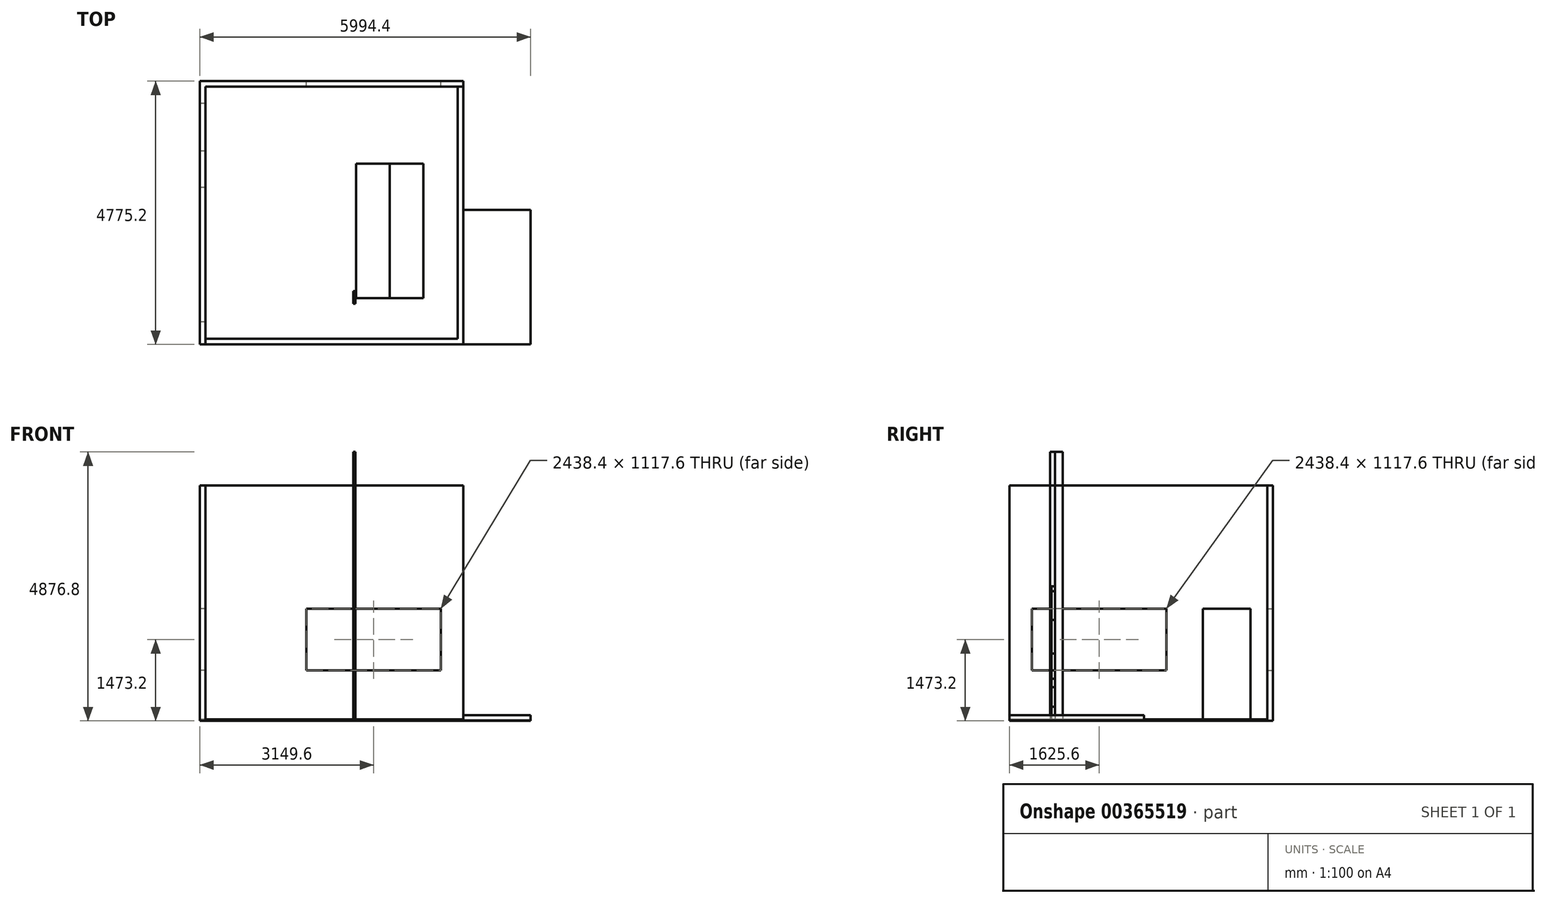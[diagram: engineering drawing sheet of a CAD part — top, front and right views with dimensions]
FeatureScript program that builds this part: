
annotation { "Feature Type Name" : "Feature", "Feature Type Description" : "" }
export const myFeature = defineFeature(function(context is Context, id is Id, definition is map)
    precondition{}
    {
        {
            var Q0;
            Q0=qCreatedBy(makeId("Top.planeOp"),FACE);
            var sketch = newSketch(context, id + "F0", { "sketchPlane" : qUnion([Q0])});
            skLineSegment(sketch, "E0.bottom", {"start": v(-51.8, 152.53) * mm, "end": v(37.1, 152.53) * mm});
            skLineSegment(sketch, "E0.top", {"start": v(-51.8, -101.47) * mm, "end": v(37.1, -101.47) * mm});
            skLineSegment(sketch, "E0.left", {"start": v(-51.8, 152.53) * mm, "end": v(-51.8, -101.47) * mm});
            skLineSegment(sketch, "E0.right", {"start": v(37.1, 152.53) * mm, "end": v(37.1, -101.47) * mm});
            skLineSegment(sketch, "E1", {"start": v(11.7, 152.53) * mm, "end": v(11.7, 12.83) * mm});
            skLineSegment(sketch, "E2", {"start": v(11.7, 12.83) * mm, "end": v(-51.8, 12.83) * mm});
            skLineSegment(sketch, "E3", {"start": v(-13.7, 152.53) * mm, "end": v(-13.7, 63.63) * mm});
            skLineSegment(sketch, "E4", {"start": v(-13.7, 63.63) * mm, "end": v(-51.8, 63.63) * mm});
            skLineSegment(sketch, "E5", {"start": v(-32.75, 152.53) * mm, "end": v(-32.75, 89.03) * mm});
            skLineSegment(sketch, "E6", {"start": v(-32.75, 89.03) * mm, "end": v(-51.8, 89.03) * mm});
            skLineSegment(sketch, "E7", {"start": v(-32.75, 89.03) * mm, "end": v(-32.75, 12.83) * mm});
            skPoint(sketch, "E7.endSnap0", {"position": v(-32.75, 63.63) * mm});
            skLineSegment(sketch, "E8", {"start": v(-32.75, 89.03) * mm, "end": v(-13.7, 89.03) * mm});
            skLineSegment(sketch, "E9.bottom", {"start": v(-51.8, 152.53) * mm, "end": v(-13.7, 152.53) * mm});
            skLineSegment(sketch, "E9.top", {"start": v(-51.8, 292.23) * mm, "end": v(-13.7, 292.23) * mm});
            skLineSegment(sketch, "E9.left", {"start": v(-51.8, 152.53) * mm, "end": v(-51.8, 292.23) * mm});
            skLineSegment(sketch, "E9.right", {"start": v(-13.7, 152.53) * mm, "end": v(-13.7, 292.23) * mm});
            skSolve(sketch);
        }
        {
            var Q0;
            {var subQ3=sQuery(id+"F0.wireOp",EDGE,"E5");Q0=makeQuery(id+"F0.imprint","IMPRINT",FACE,{"disambiguationData":[TD([[makeQuery(id+"F0.imprint","IMPRINT",EDGE,{"derivedFrom":subQ3}),-1.0]])]});}
            extrude(context, id + "F1", {"entities" : qUnion([Q0]), "depth" : 2438.4 * mm, "offsetDistance" : 25.4 * mm});
        }
        {
            var Q0;
            {var subQ3=sQuery(id+"F0.wireOp",EDGE,"E5");Q0=makeQuery(id+"F0.imprint","IMPRINT",FACE,{"disambiguationData":[TD([[makeQuery(id+"F0.imprint","IMPRINT",EDGE,{"derivedFrom":subQ3}),-1.0]])]});}
            var Q1;
            {var subQ3=sQuery(id+"F0.wireOp",EDGE,"E6");Q1=makeQuery(id+"F0.imprint","IMPRINT",FACE,{"disambiguationData":[TD([[makeQuery(id+"F0.imprint","IMPRINT",EDGE,{"derivedFrom":subQ3}),1.0]])]});}
            extrude(context, id + "F2", {"entities" : qUnion([Q0, Q1]), "depth" : 2438.4 * mm, "offsetDistance" : 25.4 * mm});
        }
        {
            var Q0;
            {var subQ3=sQuery(id+"F0.wireOp",EDGE,"E5");Q0=makeQuery(id+"F0.imprint","IMPRINT",FACE,{"disambiguationData":[TD([[makeQuery(id+"F0.imprint","IMPRINT",EDGE,{"derivedFrom":subQ3}),-1.0]])]});}
            var Q1;
            {var subQ3=sQuery(id+"F0.wireOp",EDGE,"E5");Q1=makeQuery(id+"F0.imprint","IMPRINT",FACE,{"disambiguationData":[TD([[makeQuery(id+"F0.imprint","IMPRINT",EDGE,{"derivedFrom":subQ3}),1.0]])]});}
            extrude(context, id + "F3", {"entities" : qUnion([Q0, Q1]), "depth" : 2438.4 * mm, "offsetDistance" : 25.4 * mm});
        }
        {
            var Q0;
            {var subQ3=sQuery(id+"F0.wireOp",EDGE,"E5");Q0=makeQuery(id+"F0.imprint","IMPRINT",FACE,{"disambiguationData":[TD([[makeQuery(id+"F0.imprint","IMPRINT",EDGE,{"derivedFrom":subQ3}),-1.0]])]});}
            var Q1;
            {var subQ3=sQuery(id+"F0.wireOp",EDGE,"E5");Q1=makeQuery(id+"F0.imprint","IMPRINT",FACE,{"disambiguationData":[TD([[makeQuery(id+"F0.imprint","IMPRINT",EDGE,{"derivedFrom":subQ3}),1.0]])]});}
            var Q2;
            {var subQ3=sQuery(id+"F0.wireOp",EDGE,"E6");Q2=makeQuery(id+"F0.imprint","IMPRINT",FACE,{"disambiguationData":[TD([[makeQuery(id+"F0.imprint","IMPRINT",EDGE,{"derivedFrom":subQ3}),1.0]])]});}
            var Q3;
            {var subQ3=sQuery(id+"F0.wireOp",EDGE,"E8");Q3=makeQuery(id+"F0.imprint","IMPRINT",FACE,{"disambiguationData":[TD([[makeQuery(id+"F0.imprint","IMPRINT",EDGE,{"derivedFrom":subQ3}),-1.0]])]});}
            extrude(context, id + "F4", {"entities" : qUnion([Q0, Q1, Q2, Q3]), "depth" : 2438.4 * mm, "offsetDistance" : 25.4 * mm});
        }
        {
            var Q0;
            {var subQ3=sQuery(id+"F0.wireOp",EDGE,"E5");Q0=makeQuery(id+"F0.imprint","IMPRINT",FACE,{"disambiguationData":[TD([[makeQuery(id+"F0.imprint","IMPRINT",EDGE,{"derivedFrom":subQ3}),-1.0]])]});}
            var Q1;
            {var subQ3=sQuery(id+"F0.wireOp",EDGE,"E5");Q1=makeQuery(id+"F0.imprint","IMPRINT",FACE,{"disambiguationData":[TD([[makeQuery(id+"F0.imprint","IMPRINT",EDGE,{"derivedFrom":subQ3}),1.0]])]});}
            var Q2;
            {var subQ3=sQuery(id+"F0.wireOp",EDGE,"E8");Q2=makeQuery(id+"F0.imprint","IMPRINT",FACE,{"disambiguationData":[TD([[makeQuery(id+"F0.imprint","IMPRINT",EDGE,{"derivedFrom":subQ3}),-1.0]])]});}
            var Q3;
            {var subQ3=sQuery(id+"F0.wireOp",EDGE,"E6");Q3=makeQuery(id+"F0.imprint","IMPRINT",FACE,{"disambiguationData":[TD([[makeQuery(id+"F0.imprint","IMPRINT",EDGE,{"derivedFrom":subQ3}),1.0]])]});}
            extrude(context, id + "F5", {"entities" : qUnion([Q0, Q1, Q2, Q3]), "depth" : 914.4 * mm, "offsetDistance" : 25.4 * mm});
        }
        {
            var Q0;
            {var subQ3=sQuery(id+"F0.wireOp",EDGE,"E5");Q0=makeQuery(id+"F0.imprint","IMPRINT",FACE,{"disambiguationData":[TD([[makeQuery(id+"F0.imprint","IMPRINT",EDGE,{"derivedFrom":subQ3}),-1.0]])]});}
            var Q1;
            {var subQ3=sQuery(id+"F0.wireOp",EDGE,"E5");Q1=makeQuery(id+"F0.imprint","IMPRINT",FACE,{"disambiguationData":[TD([[makeQuery(id+"F0.imprint","IMPRINT",EDGE,{"derivedFrom":subQ3}),1.0]])]});}
            var Q2;
            {var subQ3=sQuery(id+"F0.wireOp",EDGE,"E8");Q2=makeQuery(id+"F0.imprint","IMPRINT",FACE,{"disambiguationData":[TD([[makeQuery(id+"F0.imprint","IMPRINT",EDGE,{"derivedFrom":subQ3}),-1.0]])]});}
            var Q3;
            {var subQ3=sQuery(id+"F0.wireOp",EDGE,"E6");Q3=makeQuery(id+"F0.imprint","IMPRINT",FACE,{"disambiguationData":[TD([[makeQuery(id+"F0.imprint","IMPRINT",EDGE,{"derivedFrom":subQ3}),1.0]])]});}
            extrude(context, id + "F6", {"entities" : qUnion([Q0, Q1, Q2, Q3]), "depth" : 1219.2 * mm, "offsetDistance" : 25.4 * mm});
        }
        {
            var Q0;
            {var subQ3=sQuery(id+"F0.wireOp",EDGE,"E5");Q0=makeQuery(id+"F0.imprint","IMPRINT",FACE,{"disambiguationData":[TD([[makeQuery(id+"F0.imprint","IMPRINT",EDGE,{"derivedFrom":subQ3}),-1.0]])]});}
            var Q1;
            {var subQ3=sQuery(id+"F0.wireOp",EDGE,"E5");Q1=makeQuery(id+"F0.imprint","IMPRINT",FACE,{"disambiguationData":[TD([[makeQuery(id+"F0.imprint","IMPRINT",EDGE,{"derivedFrom":subQ3}),1.0]])]});}
            var Q2;
            {var subQ3=sQuery(id+"F0.wireOp",EDGE,"E8");Q2=makeQuery(id+"F0.imprint","IMPRINT",FACE,{"disambiguationData":[TD([[makeQuery(id+"F0.imprint","IMPRINT",EDGE,{"derivedFrom":subQ3}),-1.0]])]});}
            var Q3;
            {var subQ3=sQuery(id+"F0.wireOp",EDGE,"E6");Q3=makeQuery(id+"F0.imprint","IMPRINT",FACE,{"disambiguationData":[TD([[makeQuery(id+"F0.imprint","IMPRINT",EDGE,{"derivedFrom":subQ3}),1.0]])]});}
            extrude(context, id + "F7", {"entities" : qUnion([Q0, Q1, Q2, Q3]), "depth" : 1828.8 * mm, "offsetDistance" : 25.4 * mm});
        }
        {
            var Q0;
            {var subQ3=sQuery(id+"F0.wireOp",EDGE,"E5");Q0=makeQuery(id+"F0.imprint","IMPRINT",FACE,{"disambiguationData":[TD([[makeQuery(id+"F0.imprint","IMPRINT",EDGE,{"derivedFrom":subQ3}),-1.0]])]});}
            var Q1;
            {var subQ3=sQuery(id+"F0.wireOp",EDGE,"E5");Q1=makeQuery(id+"F0.imprint","IMPRINT",FACE,{"disambiguationData":[TD([[makeQuery(id+"F0.imprint","IMPRINT",EDGE,{"derivedFrom":subQ3}),1.0]])]});}
            var Q2;
            {var subQ3=sQuery(id+"F0.wireOp",EDGE,"E8");Q2=makeQuery(id+"F0.imprint","IMPRINT",FACE,{"disambiguationData":[TD([[makeQuery(id+"F0.imprint","IMPRINT",EDGE,{"derivedFrom":subQ3}),-1.0]])]});}
            var Q3;
            {var subQ3=sQuery(id+"F0.wireOp",EDGE,"E6");Q3=makeQuery(id+"F0.imprint","IMPRINT",FACE,{"disambiguationData":[TD([[makeQuery(id+"F0.imprint","IMPRINT",EDGE,{"derivedFrom":subQ3}),1.0]])]});}
            extrude(context, id + "F8", {"entities" : qUnion([Q0, Q1, Q2, Q3]), "depth" : 609.6 * mm, "offsetDistance" : 25.4 * mm});
        }
        {
            var Q0;
            {var subQ3=sQuery(id+"F0.wireOp",EDGE,"E5");Q0=makeQuery(id+"F0.imprint","IMPRINT",FACE,{"disambiguationData":[TD([[makeQuery(id+"F0.imprint","IMPRINT",EDGE,{"derivedFrom":subQ3}),-1.0]])]});}
            var Q1;
            {var subQ3=sQuery(id+"F0.wireOp",EDGE,"E5");Q1=makeQuery(id+"F0.imprint","IMPRINT",FACE,{"disambiguationData":[TD([[makeQuery(id+"F0.imprint","IMPRINT",EDGE,{"derivedFrom":subQ3}),1.0]])]});}
            extrude(context, id + "F9", {"entities" : qUnion([Q0, Q1]), "depth" : 1828.8 * mm, "offsetDistance" : 25.4 * mm});
        }
        {
            var Q0;
            {var subQ3=sQuery(id+"F0.wireOp",EDGE,"E5");Q0=makeQuery(id+"F0.imprint","IMPRINT",FACE,{"disambiguationData":[TD([[makeQuery(id+"F0.imprint","IMPRINT",EDGE,{"derivedFrom":subQ3}),-1.0]])]});}
            var Q1;
            {var subQ3=sQuery(id+"F0.wireOp",EDGE,"E5");Q1=makeQuery(id+"F0.imprint","IMPRINT",FACE,{"disambiguationData":[TD([[makeQuery(id+"F0.imprint","IMPRINT",EDGE,{"derivedFrom":subQ3}),1.0]])]});}
            extrude(context, id + "F10", {"entities" : qUnion([Q0, Q1]), "depth" : 1219.2 * mm, "offsetDistance" : 25.4 * mm});
        }
        {
            var Q0;
            {var subQ3=sQuery(id+"F0.wireOp",EDGE,"E5");Q0=makeQuery(id+"F0.imprint","IMPRINT",FACE,{"disambiguationData":[TD([[makeQuery(id+"F0.imprint","IMPRINT",EDGE,{"derivedFrom":subQ3}),-1.0]])]});}
            var Q1;
            {var subQ3=sQuery(id+"F0.wireOp",EDGE,"E5");Q1=makeQuery(id+"F0.imprint","IMPRINT",FACE,{"disambiguationData":[TD([[makeQuery(id+"F0.imprint","IMPRINT",EDGE,{"derivedFrom":subQ3}),1.0]])]});}
            extrude(context, id + "F11", {"entities" : qUnion([Q0, Q1]), "depth" : 914.4 * mm, "offsetDistance" : 25.4 * mm});
        }
        {
            var Q0;
            {var subQ3=sQuery(id+"F0.wireOp",EDGE,"E5");Q0=makeQuery(id+"F0.imprint","IMPRINT",FACE,{"disambiguationData":[TD([[makeQuery(id+"F0.imprint","IMPRINT",EDGE,{"derivedFrom":subQ3}),-1.0]])]});}
            var Q1;
            {var subQ3=sQuery(id+"F0.wireOp",EDGE,"E5");Q1=makeQuery(id+"F0.imprint","IMPRINT",FACE,{"disambiguationData":[TD([[makeQuery(id+"F0.imprint","IMPRINT",EDGE,{"derivedFrom":subQ3}),1.0]])]});}
            extrude(context, id + "F12", {"entities" : qUnion([Q0, Q1]), "depth" : 609.6 * mm, "offsetDistance" : 25.4 * mm});
        }
        {
            var Q0;
            {var subQ3=sQuery(id+"F0.wireOp",EDGE,"E5");Q0=makeQuery(id+"F0.imprint","IMPRINT",FACE,{"disambiguationData":[TD([[makeQuery(id+"F0.imprint","IMPRINT",EDGE,{"derivedFrom":subQ3}),-1.0]])]});}
            var Q1;
            {var subQ3=sQuery(id+"F0.wireOp",EDGE,"E5");Q1=makeQuery(id+"F0.imprint","IMPRINT",FACE,{"disambiguationData":[TD([[makeQuery(id+"F0.imprint","IMPRINT",EDGE,{"derivedFrom":subQ3}),1.0]])]});}
            extrude(context, id + "F13", {"entities" : qUnion([Q0, Q1]), "depth" : 762 * mm, "offsetDistance" : 25.4 * mm});
        }
        {
            var Q0;
            {var subQ3=sQuery(id+"F0.wireOp",EDGE,"E8");Q0=makeQuery(id+"F0.imprint","IMPRINT",FACE,{"disambiguationData":[TD([[makeQuery(id+"F0.imprint","IMPRINT",EDGE,{"derivedFrom":subQ3}),-1.0]])]});}
            var Q1;
            {var subQ3=sQuery(id+"F0.wireOp",EDGE,"E6");Q1=makeQuery(id+"F0.imprint","IMPRINT",FACE,{"disambiguationData":[TD([[makeQuery(id+"F0.imprint","IMPRINT",EDGE,{"derivedFrom":subQ3}),1.0]])]});}
            extrude(context, id + "F14", {"entities" : qUnion([Q0, Q1]), "depth" : 1828.8 * mm, "offsetDistance" : 25.4 * mm});
        }
        {
            var Q0;
            Q0=qCreatedBy(makeId("Top.planeOp"),FACE);
            var sketch = newSketch(context, id + "F15", { "sketchPlane" : qUnion([Q0])});
            skLineSegment(sketch, "E10.bottom", {"start": v(-2730.57, 3997.99) * mm, "end": v(1841.43, 3997.99) * mm});
            skLineSegment(sketch, "E10.top", {"start": v(-2730.57, -574.01) * mm, "end": v(1841.43, -574.01) * mm});
            skLineSegment(sketch, "E10.left", {"start": v(-2730.57, 3997.99) * mm, "end": v(-2730.57, -574.01) * mm});
            skLineSegment(sketch, "E10.right", {"start": v(1841.43, 3997.99) * mm, "end": v(1841.43, -574.01) * mm});
            skLineSegment(sketch, "E11.bottom", {"start": v(1943.03, -675.61) * mm, "end": v(3162.23, -675.61) * mm});
            skLineSegment(sketch, "E11.top", {"start": v(1943.03, 1762.79) * mm, "end": v(3162.23, 1762.79) * mm});
            skLineSegment(sketch, "E11.right", {"start": v(3162.23, -675.61) * mm, "end": v(3162.23, 1762.79) * mm});
            skLineSegment(sketch, "E12.0", {"start": v(-2832.17, 4099.59) * mm, "end": v(-2832.17, -675.61) * mm});
            skLineSegment(sketch, "E12.1", {"start": v(-2832.17, 4099.59) * mm, "end": v(1943.03, 4099.59) * mm});
            skLineSegment(sketch, "E12.2", {"start": v(1943.03, 4099.59) * mm, "end": v(1943.03, -675.61) * mm});
            skLineSegment(sketch, "E12.3", {"start": v(-2832.17, -675.61) * mm, "end": v(1943.03, -675.61) * mm});
            skLineSegment(sketch, "E13", {"start": v(-2730.57, 3693.19) * mm, "end": v(-2832.17, 3693.19) * mm});
            skLineSegment(sketch, "E14.0", {"start": v(-2730.57, 2829.59) * mm, "end": v(-2832.17, 2829.59) * mm});
            skLineSegment(sketch, "E15", {"start": v(1841.43, 3997.99) * mm, "end": v(1943.03, 3997.99) * mm});
            skLineSegment(sketch, "E16", {"start": v(-2730.57, -574.01) * mm, "end": v(-2730.57, -675.61) * mm});
            skLineSegment(sketch, "E17", {"start": v(-901.77, 3997.99) * mm, "end": v(-901.77, 4099.59) * mm});
            skLineSegment(sketch, "E18", {"start": v(-2730.57, 2169.19) * mm, "end": v(-2832.17, 2169.19) * mm});
            skLineSegment(sketch, "E19.0", {"start": v(1536.63, 3997.99) * mm, "end": v(1536.63, 4099.59) * mm});
            skLineSegment(sketch, "E20.0", {"start": v(-2730.57, -269.21) * mm, "end": v(-2832.17, -269.21) * mm});
            skSolve(sketch);
        }
        {
            var Q0;
            Q0=makeQuery(id+"F15.imprint","IMPRINT",FACE,{"disambiguationData":[TD([[makeQuery(id+"F15.imprint","IMPRINT",EDGE,{"derivedFrom":sQuery(id+"F15.wireOp",EDGE,"E10.bottom")}),-1.0]])]});
            var Q1;
            {var subQ0=sQuery(id+"F15.wireOp",EDGE,"E13");Q1=makeQuery(id+"F15.imprint","IMPRINT",FACE,{"disambiguationData":[TD([[makeQuery(id+"F15.imprint","IMPRINT",EDGE,{"derivedFrom":subQ0}),1.0]])]});}
            extrude(context, id + "F16", {"entities" : qUnion([Q0, Q1]), "depth" : 25.4 * mm, "offsetDistance" : 25.4 * mm});
        }
        {
            var Q0;
            Q0=makeQuery(id+"F15.imprint","IMPRINT",FACE,{"disambiguationData":[TD([[makeQuery(id+"F15.imprint","IMPRINT",EDGE,{"derivedFrom":sQuery(id+"F15.wireOp",EDGE,"E11.bottom")}),1.0]])]});
            extrude(context, id + "F17", {"entities" : qUnion([Q0]), "depth" : 6.35 * mm, "offsetDistance" : 25.4 * mm});
        }
        {
            var Q0;
            {var subQ0=sQuery(id+"F15.wireOp",EDGE,"E14.0");Q0=makeQuery(id+"F15.imprint","IMPRINT",FACE,{"disambiguationData":[TD([[makeQuery(id+"F15.imprint","IMPRINT",EDGE,{"derivedFrom":subQ0}),1.0]])]});}
            var Q1;
            {var subQ0=sQuery(id+"F15.wireOp",EDGE,"E15");Q1=makeQuery(id+"F15.imprint","IMPRINT",FACE,{"disambiguationData":[TD([[makeQuery(id+"F15.imprint","IMPRINT",EDGE,{"derivedFrom":subQ0}),1.0]])]});}
            var Q2;
            {var subQ4=sQuery(id+"F15.wireOp",EDGE,"E13");Q2=makeQuery(id+"F15.imprint","IMPRINT",FACE,{"disambiguationData":[TD([[makeQuery(id+"F15.imprint","IMPRINT",EDGE,{"derivedFrom":subQ4}),-1.0]])]});}
            var Q3;
            {var subQ0=sQuery(id+"F15.wireOp",EDGE,"E16");Q3=makeQuery(id+"F15.imprint","IMPRINT",FACE,{"disambiguationData":[TD([[makeQuery(id+"F15.imprint","IMPRINT",EDGE,{"derivedFrom":subQ0}),-1.0]])]});}
            extrude(context, id + "F18", {"entities" : qUnion([Q0, Q1, Q2, Q3]), "operationType" : NewBodyOperationType.ADD, "depth" : 4267.2 * mm, "offsetDistance" : 25.4 * mm});
        }
        {
            var Q0;
            Q0=makeQuery(id+"F15.imprint","IMPRINT",FACE,{"disambiguationData":[TD([[makeQuery(id+"F15.imprint","IMPRINT",EDGE,{"derivedFrom":sQuery(id+"F15.wireOp",EDGE,"E10.top")}),-1.0]])]});
            extrude(context, id + "F19", {"entities" : qUnion([Q0]), "operationType" : NewBodyOperationType.ADD, "depth" : 27.94 * mm, "offsetDistance" : 25.4 * mm});
        }
        {
            var Q0;
            {var subQ0=sQuery(id+"F15.wireOp",EDGE,"E13");Q0=makeQuery(id+"F15.imprint","IMPRINT",FACE,{"disambiguationData":[TD([[makeQuery(id+"F15.imprint","IMPRINT",EDGE,{"derivedFrom":subQ0}),1.0]])]});}
            var Q1;
            {var subQ0=sQuery(id+"F15.wireOp",EDGE,"E18");Q1=makeQuery(id+"F15.imprint","IMPRINT",FACE,{"disambiguationData":[TD([[makeQuery(id+"F15.imprint","IMPRINT",EDGE,{"derivedFrom":subQ0}),1.0]])]});}
            var Q2;
            {var subQ0=sQuery(id+"F15.wireOp",EDGE,"E17");Q2=makeQuery(id+"F15.imprint","IMPRINT",FACE,{"disambiguationData":[TD([[makeQuery(id+"F15.imprint","IMPRINT",EDGE,{"derivedFrom":subQ0}),-1.0]])]});}
            extrude(context, id + "F20", {"entities" : qUnion([Q0, Q1, Q2]), "operationType" : NewBodyOperationType.ADD, "depth" : 4267.2 * mm, "offsetDistance" : 25.4 * mm, "hasSecondDirection" : true, "secondDirectionOppositeDirection" : false, "secondDirectionDepth" : 2032 * mm});
        }
        {
            var Q0;
            {var subQ0=sQuery(id+"F15.wireOp",EDGE,"E18");Q0=makeQuery(id+"F15.imprint","IMPRINT",FACE,{"disambiguationData":[TD([[makeQuery(id+"F15.imprint","IMPRINT",EDGE,{"derivedFrom":subQ0}),1.0]])]});}
            var Q1;
            {var subQ0=sQuery(id+"F15.wireOp",EDGE,"E17");Q1=makeQuery(id+"F15.imprint","IMPRINT",FACE,{"disambiguationData":[TD([[makeQuery(id+"F15.imprint","IMPRINT",EDGE,{"derivedFrom":subQ0}),-1.0]])]});}
            extrude(context, id + "F21", {"entities" : qUnion([Q0, Q1]), "operationType" : NewBodyOperationType.ADD, "depth" : 914.4 * mm, "offsetDistance" : 25.4 * mm});
        }
        {
            var Q0;
            {var subQ0=sQuery(id+"F15.wireOp",EDGE,"E11.bottom");Q0=makeQuery(id+"F15.imprint","IMPRINT",FACE,{"disambiguationData":[TD([[makeQuery(id+"F15.imprint","IMPRINT",EDGE,{"derivedFrom":subQ0}),1.0]])]});}
            extrude(context, id + "F22", {"entities" : qUnion([Q0]), "depth" : 101.6 * mm, "offsetDistance" : 25.4 * mm});
        }
        {
            var Q0;
            {var subQ3=sQuery(id+"F0.wireOp",EDGE,"E5");Q0=makeQuery(id+"F0.imprint","IMPRINT",FACE,{"disambiguationData":[TD([[makeQuery(id+"F0.imprint","IMPRINT",EDGE,{"derivedFrom":subQ3}),-1.0]])]});}
            var Q1;
            {var subQ3=sQuery(id+"F0.wireOp",EDGE,"E5");Q1=makeQuery(id+"F0.imprint","IMPRINT",FACE,{"disambiguationData":[TD([[makeQuery(id+"F0.imprint","IMPRINT",EDGE,{"derivedFrom":subQ3}),1.0]])]});}
            var Q2;
            {var subQ3=sQuery(id+"F0.wireOp",EDGE,"E6");Q2=makeQuery(id+"F0.imprint","IMPRINT",FACE,{"disambiguationData":[TD([[makeQuery(id+"F0.imprint","IMPRINT",EDGE,{"derivedFrom":subQ3}),1.0]])]});}
            var Q3;
            {var subQ3=sQuery(id+"F0.wireOp",EDGE,"E8");Q3=makeQuery(id+"F0.imprint","IMPRINT",FACE,{"disambiguationData":[TD([[makeQuery(id+"F0.imprint","IMPRINT",EDGE,{"derivedFrom":subQ3}),-1.0]])]});}
            extrude(context, id + "F23", {"entities" : qUnion([Q0, Q1, Q2, Q3]), "depth" : 2352.67 * mm, "offsetDistance" : 25.4 * mm});
        }
        {
            var Q0;
            Q0=makeQuery(id+"F0.imprint","IMPRINT",FACE,{"disambiguationData":[TD([[makeQuery(id+"F0.imprint","IMPRINT",EDGE,{"derivedFrom":sQuery(id+"F0.wireOp",EDGE,"E9.top")}),-1.0]])]});
            extrude(context, id + "F24", {"entities" : qUnion([Q0]), "depth" : 4267.2 * mm, "offsetDistance" : 25.4 * mm});
        }
        {
            var Q0;
            Q0=makeQuery(id+"F0.imprint","IMPRINT",FACE,{"disambiguationData":[TD([[makeQuery(id+"F0.imprint","IMPRINT",EDGE,{"derivedFrom":sQuery(id+"F0.wireOp",EDGE,"E9.top")}),-1.0]])]});
            extrude(context, id + "F25", {"entities" : qUnion([Q0]), "depth" : 4876.8 * mm, "offsetDistance" : 25.4 * mm});
        }
        {
            var Q0;
            {var subQ3=sQuery(id+"F0.wireOp",EDGE,"E6");Q0=makeQuery(id+"F0.imprint","IMPRINT",FACE,{"disambiguationData":[TD([[makeQuery(id+"F0.imprint","IMPRINT",EDGE,{"derivedFrom":subQ3}),1.0]])]});}
            var Q1;
            {var subQ4=sQuery(id+"F0.wireOp",EDGE,"E5");Q1=makeQuery(id+"F0.imprint","IMPRINT",FACE,{"disambiguationData":[TD([[makeQuery(id+"F0.imprint","IMPRINT",EDGE,{"derivedFrom":subQ4}),-1.0]])]});}
            var Q2;
            {var subQ4=sQuery(id+"F0.wireOp",EDGE,"E5");Q2=makeQuery(id+"F0.imprint","IMPRINT",FACE,{"disambiguationData":[TD([[makeQuery(id+"F0.imprint","IMPRINT",EDGE,{"derivedFrom":subQ4}),1.0]])]});}
            var Q3;
            {var subQ3=sQuery(id+"F0.wireOp",EDGE,"E8");Q3=makeQuery(id+"F0.imprint","IMPRINT",FACE,{"disambiguationData":[TD([[makeQuery(id+"F0.imprint","IMPRINT",EDGE,{"derivedFrom":subQ3}),-1.0]])]});}
            extrude(context, id + "F26", {"entities" : qUnion([Q0, Q1, Q2, Q3]), "depth" : 254 * mm, "offsetDistance" : 25.4 * mm});
        }
        {
            var Q0;
            {var subQ3=sQuery(id+"F0.wireOp",EDGE,"E6");Q0=makeQuery(id+"F0.imprint","IMPRINT",FACE,{"disambiguationData":[TD([[makeQuery(id+"F0.imprint","IMPRINT",EDGE,{"derivedFrom":subQ3}),1.0]])]});}
            var Q1;
            {var subQ4=sQuery(id+"F0.wireOp",EDGE,"E5");Q1=makeQuery(id+"F0.imprint","IMPRINT",FACE,{"disambiguationData":[TD([[makeQuery(id+"F0.imprint","IMPRINT",EDGE,{"derivedFrom":subQ4}),-1.0]])]});}
            var Q2;
            {var subQ4=sQuery(id+"F0.wireOp",EDGE,"E5");Q2=makeQuery(id+"F0.imprint","IMPRINT",FACE,{"disambiguationData":[TD([[makeQuery(id+"F0.imprint","IMPRINT",EDGE,{"derivedFrom":subQ4}),1.0]])]});}
            var Q3;
            {var subQ3=sQuery(id+"F0.wireOp",EDGE,"E8");Q3=makeQuery(id+"F0.imprint","IMPRINT",FACE,{"disambiguationData":[TD([[makeQuery(id+"F0.imprint","IMPRINT",EDGE,{"derivedFrom":subQ3}),-1.0]])]});}
            extrude(context, id + "F27", {"entities" : qUnion([Q0, Q1, Q2, Q3]), "depth" : 101.6 * mm, "offsetDistance" : 25.4 * mm});
        }
        {
            var Q0;
            {var subQ3=sQuery(id+"F0.wireOp",EDGE,"E6");Q0=makeQuery(id+"F0.imprint","IMPRINT",FACE,{"disambiguationData":[TD([[makeQuery(id+"F0.imprint","IMPRINT",EDGE,{"derivedFrom":subQ3}),1.0]])]});}
            var Q1;
            {var subQ4=sQuery(id+"F0.wireOp",EDGE,"E5");Q1=makeQuery(id+"F0.imprint","IMPRINT",FACE,{"disambiguationData":[TD([[makeQuery(id+"F0.imprint","IMPRINT",EDGE,{"derivedFrom":subQ4}),-1.0]])]});}
            var Q2;
            {var subQ4=sQuery(id+"F0.wireOp",EDGE,"E5");Q2=makeQuery(id+"F0.imprint","IMPRINT",FACE,{"disambiguationData":[TD([[makeQuery(id+"F0.imprint","IMPRINT",EDGE,{"derivedFrom":subQ4}),1.0]])]});}
            var Q3;
            {var subQ3=sQuery(id+"F0.wireOp",EDGE,"E8");Q3=makeQuery(id+"F0.imprint","IMPRINT",FACE,{"disambiguationData":[TD([[makeQuery(id+"F0.imprint","IMPRINT",EDGE,{"derivedFrom":subQ3}),-1.0]])]});}
            extrude(context, id + "F28", {"entities" : qUnion([Q0, Q1, Q2, Q3]), "depth" : 4876.8 * mm, "offsetDistance" : 25.4 * mm});
        }
        {
            var Q0;
            {var subQ4=sQuery(id+"F0.wireOp",EDGE,"E5");Q0=makeQuery(id+"F0.imprint","IMPRINT",FACE,{"disambiguationData":[TD([[makeQuery(id+"F0.imprint","IMPRINT",EDGE,{"derivedFrom":subQ4}),-1.0]])]});}
            var Q1;
            {var subQ4=sQuery(id+"F0.wireOp",EDGE,"E5");Q1=makeQuery(id+"F0.imprint","IMPRINT",FACE,{"disambiguationData":[TD([[makeQuery(id+"F0.imprint","IMPRINT",EDGE,{"derivedFrom":subQ4}),1.0]])]});}
            var Q2;
            {var subQ3=sQuery(id+"F0.wireOp",EDGE,"E8");Q2=makeQuery(id+"F0.imprint","IMPRINT",FACE,{"disambiguationData":[TD([[makeQuery(id+"F0.imprint","IMPRINT",EDGE,{"derivedFrom":subQ3}),-1.0]])]});}
            var Q3;
            {var subQ3=sQuery(id+"F0.wireOp",EDGE,"E6");Q3=makeQuery(id+"F0.imprint","IMPRINT",FACE,{"disambiguationData":[TD([[makeQuery(id+"F0.imprint","IMPRINT",EDGE,{"derivedFrom":subQ3}),1.0]])]});}
            extrude(context, id + "F29", {"entities" : qUnion([Q0, Q1, Q2, Q3]), "depth" : 4267.2 * mm, "offsetDistance" : 25.4 * mm});
        }
        {
            var Q0;
            Q0=qCreatedBy(makeId("Top.planeOp"),FACE);
            var sketch = newSketch(context, id + "F30", { "sketchPlane" : qUnion([Q0])});
            skLineSegment(sketch, "E21.bottom", {"start": v(0, 166.64) * mm, "end": v(1219.2, 166.64) * mm});
            skLineSegment(sketch, "E21.top", {"start": v(0, 2605.04) * mm, "end": v(1219.2, 2605.04) * mm});
            skLineSegment(sketch, "E21.left", {"start": v(0, 166.64) * mm, "end": v(0, 2605.04) * mm});
            skLineSegment(sketch, "E21.right", {"start": v(1219.2, 166.64) * mm, "end": v(1219.2, 2605.04) * mm});
            skLineSegment(sketch, "E22", {"start": v(609.6, 2605.04) * mm, "end": v(609.6, 166.64) * mm});
            skSolve(sketch);
        }
        {
            var Q0;
            {var subQ0=sQuery(id+"F30.wireOp",EDGE,"E21.left");Q0=makeQuery(id+"F30.imprint","IMPRINT",FACE,{"disambiguationData":[TD([[makeQuery(id+"F30.imprint","IMPRINT",EDGE,{"derivedFrom":subQ0}),-1.0]])]});}
            extrude(context, id + "F31", {"entities" : qUnion([Q0]), "depth" : 25.4 * mm, "offsetDistance" : 25.4 * mm});
        }
        {
            var Q0;
            {var subQ0=sQuery(id+"F30.wireOp",EDGE,"E21.left");Q0=makeQuery(id+"F30.imprint","IMPRINT",FACE,{"disambiguationData":[TD([[makeQuery(id+"F30.imprint","IMPRINT",EDGE,{"derivedFrom":subQ0}),-1.0]])]});}
            var Q1;
            {var subQ0=sQuery(id+"F30.wireOp",EDGE,"E21.right");Q1=makeQuery(id+"F30.imprint","IMPRINT",FACE,{"disambiguationData":[TD([[makeQuery(id+"F30.imprint","IMPRINT",EDGE,{"derivedFrom":subQ0}),1.0]])]});}
            extrude(context, id + "F32", {"entities" : qUnion([Q0, Q1]), "depth" : 25.4 * mm, "offsetDistance" : 25.4 * mm});
        }
    });
